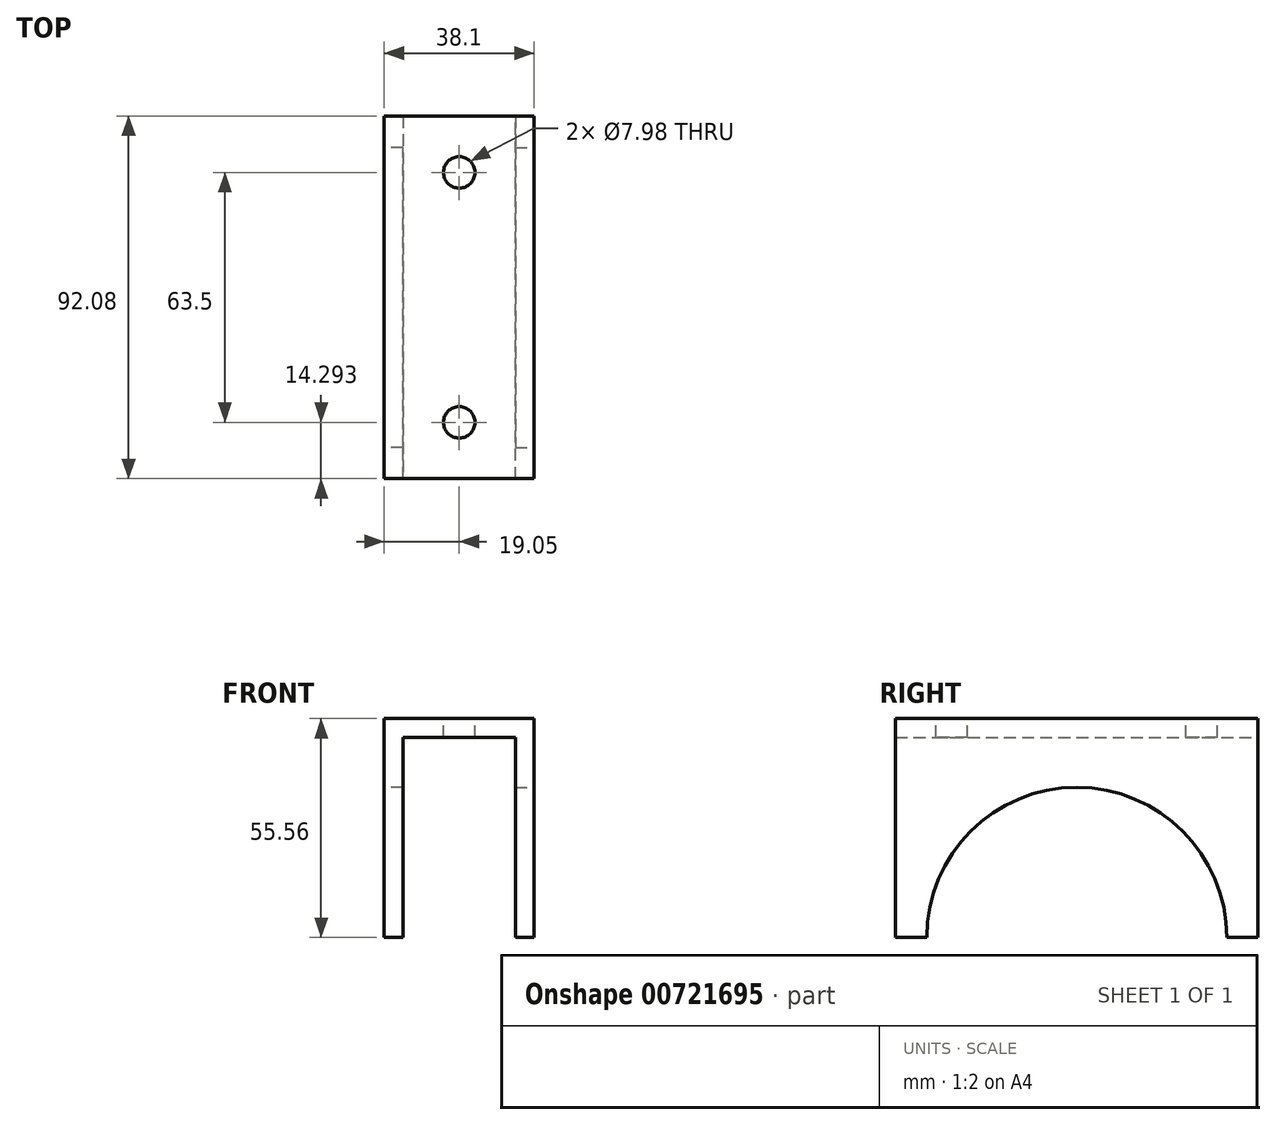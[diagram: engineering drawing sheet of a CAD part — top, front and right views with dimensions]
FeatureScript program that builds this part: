
annotation { "Feature Type Name" : "Feature", "Feature Type Description" : "" }
export const myFeature = defineFeature(function(context is Context, id is Id, definition is map)
    precondition{}
    {
        {
            var Q0;
            Q0=qCreatedBy(makeId("Top.planeOp"),FACE);
            var sketch = newSketch(context, id + "F0", { "sketchPlane" : qUnion([Q0])});
            skLineSegment(sketch, "E0.MirrorCS", {"start": v(19.05, 0) * mm, "end": v(-19.05, 0) * mm});
            skLineSegment(sketch, "E1.MirrorCS", {"start": v(19.05, -92.08) * mm, "end": v(-19.05, -92.08) * mm});
            skLineSegment(sketch, "E2.MirrorCS", {"start": v(19.05, 0) * mm, "end": v(19.05, -92.08) * mm});
            skLineSegment(sketch, "E3.MirrorCS", {"start": v(-19.05, 0) * mm, "end": v(-19.05, -92.08) * mm});
            skSolve(sketch);
        }
        {
            var Q0;
            Q0=qSketchRegion(id+"F0",true);
            extrude(context, id + "F1", {"entities" : qUnion([Q0]), "oppositeDirection" : true, "depth" : 4.76 * mm, "offsetDistance" : 25.4 * mm});
        }
        {
            var Q0;
            Q0=makeQuery(id+"F1.opExtrude","SWEPT_FACE",FACE,{"disambiguationData":[OSD([sQuery(id+"F0.wireOp",EDGE,"E3.MirrorCS")])]});
            var sketch = newSketch(context, id + "F2", { "sketchPlane" : qUnion([Q0])});
            skLineSegment(sketch, "E4", {"start": v(0, 0) * mm, "end": v(0, -55.56) * mm});
            skLineSegment(sketch, "E5", {"start": v(0, 0) * mm, "end": v(92.08, 0) * mm});
            skLineSegment(sketch, "E6", {"start": v(92.08, 0) * mm, "end": v(92.08, -55.56) * mm});
            skLineSegment(sketch, "E7", {"start": v(46.04, 0) * mm, "end": v(46.04, -88.6) * mm, "construction": true});
            skArc(sketch, "E8", {"start": v(84.14, -55.56) * mm, "mid": v(46.04, -17.46) * mm, "end": v(7.94, -55.56) * mm});
            skLineSegment(sketch, "E9", {"start": v(0, -55.56) * mm, "end": v(7.94, -55.56) * mm});
            skLineSegment(sketch, "E10", {"start": v(92.08, -55.56) * mm, "end": v(84.14, -55.56) * mm});
            skSolve(sketch);
        }
        {
            var Q0;
            Q0=qSketchRegion(id+"F2",true);
            extrude(context, id + "F3", {"entities" : qUnion([Q0]), "operationType" : NewBodyOperationType.ADD, "oppositeDirection" : true, "depth" : 4.76 * mm, "offsetDistance" : 25.4 * mm});
        }
        {
            var Q0;
            Q0=makeQuery(id+"F1.opExtrude","SWEPT_FACE",FACE,{"disambiguationData":[OSD([sQuery(id+"F0.wireOp",EDGE,"E2.MirrorCS")])]});
            var sketch = newSketch(context, id + "F4", { "sketchPlane" : qUnion([Q0])});
            skLineSegment(sketch, "E11", {"start": v(-92.08, 0) * mm, "end": v(-92.08, -55.56) * mm});
            skLineSegment(sketch, "E12", {"start": v(-46.04, 0) * mm, "end": v(-46.04, -45.41) * mm, "construction": true});
            skLineSegment(sketch, "E13.MirrorCS", {"start": v(0, 0) * mm, "end": v(0, -55.56) * mm});
            skLineSegment(sketch, "E14", {"start": v(0, 0) * mm, "end": v(-92.08, 0) * mm});
            skArc(sketch, "E15", {"start": v(-7.94, -55.56) * mm, "mid": v(-46.04, -17.46) * mm, "end": v(-84.14, -55.56) * mm});
            skLineSegment(sketch, "E16", {"start": v(0, -55.56) * mm, "end": v(-7.94, -55.56) * mm});
            skLineSegment(sketch, "E17", {"start": v(-92.08, -55.56) * mm, "end": v(-84.14, -55.56) * mm});
            skSolve(sketch);
        }
        {
            var Q0;
            Q0 = qSketchRegion(id + "F4", true);
            extrude(context, id + "F5", {"entities" : qUnion([Q0]), "operationType" : NewBodyOperationType.ADD, "oppositeDirection" : true, "depth" : 4.76 * mm, "offsetDistance" : 25.4 * mm});
        }
        {
            var Q0;
            Q0=qCreatedBy(makeId("Top.planeOp"),FACE);
            var sketch = newSketch(context, id + "F6", { "sketchPlane" : qUnion([Q0])});
            skLineSegment(sketch, "E18", {"start": v(0, 0) * mm, "end": v(0, -92.08) * mm, "construction": true});
            skLineSegment(sketch, "E19", {"start": v(-19.05, -46.04) * mm, "end": v(19.05, -46.04) * mm, "construction": true});
            skCircle(sketch, "E20", {"center": v(0, -14.29) * mm, "radius": 3.99 * mm});
            skCircle(sketch, "E21.MirrorC", {"center": v(0, -77.79) * mm, "radius": 3.99 * mm});
            skSolve(sketch);
        }
        {
            var Q0;
            Q0=qSketchRegion(id+"F6",true);
            extrude(context, id + "F7", {"entities" : qUnion([Q0]), "operationType" : NewBodyOperationType.REMOVE, "endBound" : BoundingType.THROUGH_ALL, "oppositeDirection" : true, "depth" : 25.4 * mm, "offsetDistance" : 25.4 * mm});
        }
    });
